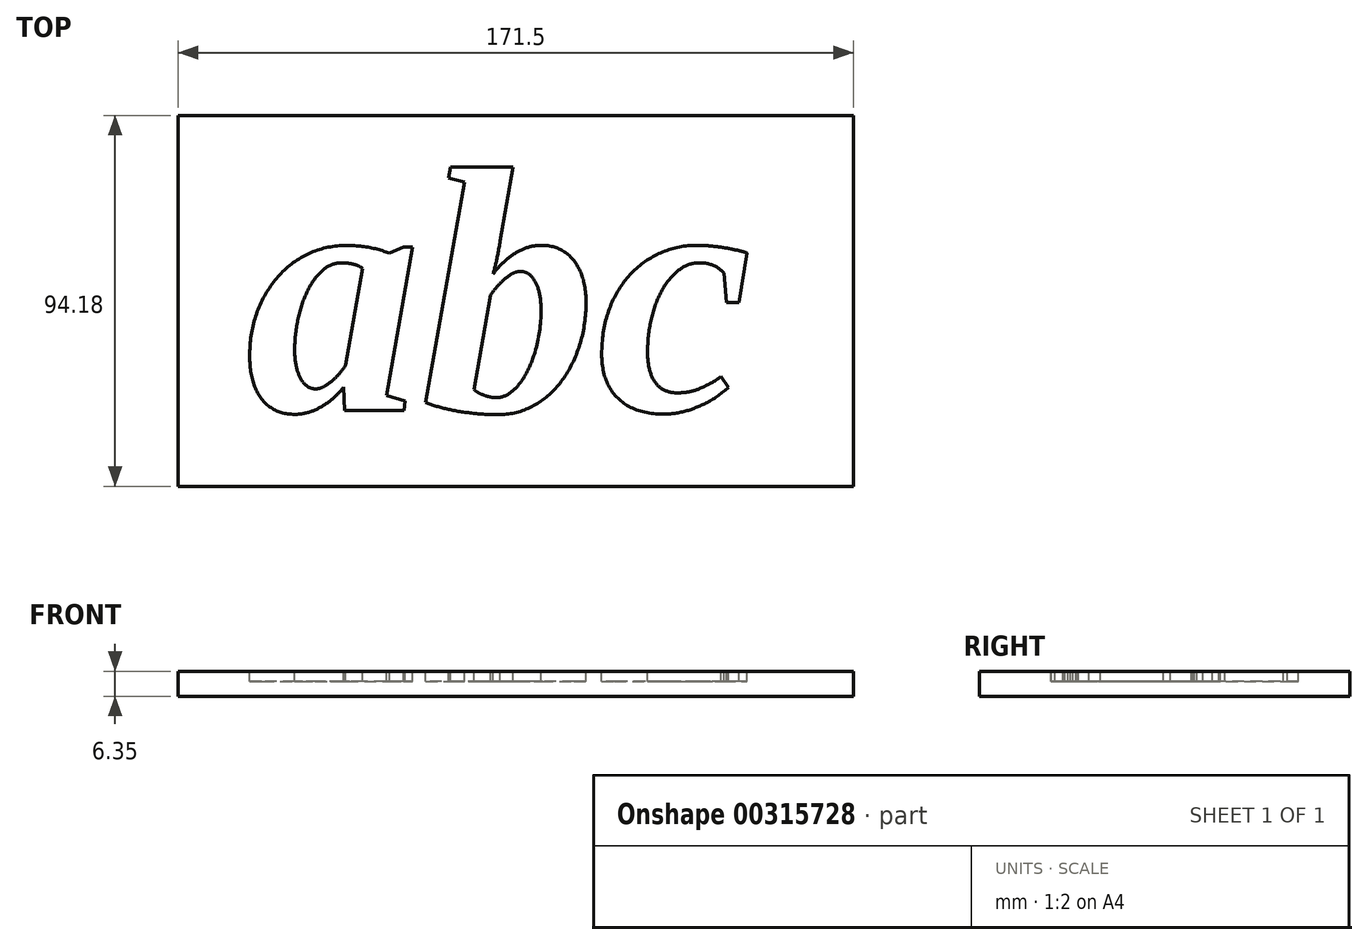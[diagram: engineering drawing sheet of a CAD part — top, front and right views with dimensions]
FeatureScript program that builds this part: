
annotation { "Feature Type Name" : "Feature", "Feature Type Description" : "" }
export const myFeature = defineFeature(function(context is Context, id is Id, definition is map)
    precondition{}
    {
        {
            var Q0;
            Q0=qCreatedBy(makeId("Top.planeOp"),FACE);
            var sketch = newSketch(context, id + "F0", { "sketchPlane" : qUnion([Q0])});
            skText(sketch, "E0", { "text": "abc", "fontName": "Tinos-BoldItalic.ttf"});
            const initialGuessF0  = {"E0": [-0.06912, -0.03573, 1, 0, 0.0642]};
            skSetInitialGuess(sketch, initialGuessF0);
            skSolve(sketch);
        }
        {
            var Q0;
            Q0 = qSketchRegion(id + "F0", true);
            extrude(context, id + "F1", {"entities" : qUnion([Q0]), "oppositeDirection" : true, "depth" : 2.54 * mm});
        }
        {
            var Q0;
            Q0=qCreatedBy(makeId("Top.planeOp"),FACE);
            var sketch = newSketch(context, id + "F2", { "sketchPlane" : qUnion([Q0])});
            skLineSegment(sketch, "E1.bottom", {"start": v(-86.22, 39.24) * mm, "end": v(85.28, 39.24) * mm});
            skLineSegment(sketch, "E1.top", {"start": v(-86.22, -54.94) * mm, "end": v(85.28, -54.94) * mm});
            skLineSegment(sketch, "E1.left", {"start": v(-86.22, 39.24) * mm, "end": v(-86.22, -54.94) * mm});
            skLineSegment(sketch, "E1.right", {"start": v(85.28, 39.24) * mm, "end": v(85.28, -54.94) * mm});
            skSolve(sketch);
        }
        {
            var Q0;
            Q0 = qSketchRegion(id + "F2", true);
            extrude(context, id + "F3", {"entities" : qUnion([Q0]), "oppositeDirection" : true, "depth" : 6.35 * mm});
        }
        {
            var Q0;
            Q0=makeQuery(id+"F1.opExtrude","SWEPT_BODY",BODY,{"disambiguationData":[OSD([sQuery(id+"F0.wireOp",EDGE,"E0.sketch_text.stroke-0"),sQuery(id+"F0.wireOp",EDGE,"E0.sketch_text.stroke-1"),sQuery(id+"F0.wireOp",EDGE,"E0.sketch_text.stroke-2"),sQuery(id+"F0.wireOp",EDGE,"E0.sketch_text.stroke-3"),sQuery(id+"F0.wireOp",EDGE,"E0.sketch_text.stroke-4"),sQuery(id+"F0.wireOp",EDGE,"E0.sketch_text.stroke-5"),sQuery(id+"F0.wireOp",EDGE,"E0.sketch_text.stroke-6"),sQuery(id+"F0.wireOp",EDGE,"E0.sketch_text.stroke-7"),sQuery(id+"F0.wireOp",EDGE,"E0.sketch_text.stroke-8"),sQuery(id+"F0.wireOp",EDGE,"E0.sketch_text.stroke-9"),sQuery(id+"F0.wireOp",EDGE,"E0.sketch_text.stroke-10"),sQuery(id+"F0.wireOp",EDGE,"E0.sketch_text.stroke-11"),sQuery(id+"F0.wireOp",EDGE,"E0.sketch_text.stroke-12"),sQuery(id+"F0.wireOp",EDGE,"E0.sketch_text.stroke-13"),sQuery(id+"F0.wireOp",EDGE,"E0.sketch_text.stroke-14"),sQuery(id+"F0.wireOp",EDGE,"E0.sketch_text.stroke-15"),sQuery(id+"F0.wireOp",EDGE,"E0.sketch_text.stroke-16"),sQuery(id+"F0.wireOp",EDGE,"E0.sketch_text.stroke-17"),sQuery(id+"F0.wireOp",EDGE,"E0.sketch_text.stroke-18"),sQuery(id+"F0.wireOp",EDGE,"E0.sketch_text.stroke-19"),sQuery(id+"F0.wireOp",EDGE,"E0.sketch_text.stroke-20"),sQuery(id+"F0.wireOp",EDGE,"E0.sketch_text.stroke-21"),sQuery(id+"F0.wireOp",EDGE,"E0.sketch_text.stroke-22"),sQuery(id+"F0.wireOp",EDGE,"E0.sketch_text.stroke-23")])]});
            var Q1;
            Q1=makeQuery(id+"F1.opExtrude","SWEPT_BODY",BODY,{"disambiguationData":[OSD([sQuery(id+"F0.wireOp",EDGE,"E0.sketch_text.stroke-24"),sQuery(id+"F0.wireOp",EDGE,"E0.sketch_text.stroke-25"),sQuery(id+"F0.wireOp",EDGE,"E0.sketch_text.stroke-26"),sQuery(id+"F0.wireOp",EDGE,"E0.sketch_text.stroke-27"),sQuery(id+"F0.wireOp",EDGE,"E0.sketch_text.stroke-28"),sQuery(id+"F0.wireOp",EDGE,"E0.sketch_text.stroke-29"),sQuery(id+"F0.wireOp",EDGE,"E0.sketch_text.stroke-30"),sQuery(id+"F0.wireOp",EDGE,"E0.sketch_text.stroke-31"),sQuery(id+"F0.wireOp",EDGE,"E0.sketch_text.stroke-32"),sQuery(id+"F0.wireOp",EDGE,"E0.sketch_text.stroke-33"),sQuery(id+"F0.wireOp",EDGE,"E0.sketch_text.stroke-34"),sQuery(id+"F0.wireOp",EDGE,"E0.sketch_text.stroke-35"),sQuery(id+"F0.wireOp",EDGE,"E0.sketch_text.stroke-36"),sQuery(id+"F0.wireOp",EDGE,"E0.sketch_text.stroke-37"),sQuery(id+"F0.wireOp",EDGE,"E0.sketch_text.stroke-38"),sQuery(id+"F0.wireOp",EDGE,"E0.sketch_text.stroke-39"),sQuery(id+"F0.wireOp",EDGE,"E0.sketch_text.stroke-40"),sQuery(id+"F0.wireOp",EDGE,"E0.sketch_text.stroke-41"),sQuery(id+"F0.wireOp",EDGE,"E0.sketch_text.stroke-42"),sQuery(id+"F0.wireOp",EDGE,"E0.sketch_text.stroke-43"),sQuery(id+"F0.wireOp",EDGE,"E0.sketch_text.stroke-44"),sQuery(id+"F0.wireOp",EDGE,"E0.sketch_text.stroke-45"),sQuery(id+"F0.wireOp",EDGE,"E0.sketch_text.stroke-46"),sQuery(id+"F0.wireOp",EDGE,"E0.sketch_text.stroke-47"),sQuery(id+"F0.wireOp",EDGE,"E0.sketch_text.stroke-48")])]});
            var Q2;
            Q2=makeQuery(id+"F1.opExtrude","SWEPT_BODY",BODY,{"disambiguationData":[OSD([sQuery(id+"F0.wireOp",EDGE,"E0.sketch_text.stroke-49"),sQuery(id+"F0.wireOp",EDGE,"E0.sketch_text.stroke-50"),sQuery(id+"F0.wireOp",EDGE,"E0.sketch_text.stroke-51"),sQuery(id+"F0.wireOp",EDGE,"E0.sketch_text.stroke-52"),sQuery(id+"F0.wireOp",EDGE,"E0.sketch_text.stroke-53"),sQuery(id+"F0.wireOp",EDGE,"E0.sketch_text.stroke-54"),sQuery(id+"F0.wireOp",EDGE,"E0.sketch_text.stroke-55"),sQuery(id+"F0.wireOp",EDGE,"E0.sketch_text.stroke-56"),sQuery(id+"F0.wireOp",EDGE,"E0.sketch_text.stroke-57"),sQuery(id+"F0.wireOp",EDGE,"E0.sketch_text.stroke-58"),sQuery(id+"F0.wireOp",EDGE,"E0.sketch_text.stroke-59"),sQuery(id+"F0.wireOp",EDGE,"E0.sketch_text.stroke-60"),sQuery(id+"F0.wireOp",EDGE,"E0.sketch_text.stroke-61"),sQuery(id+"F0.wireOp",EDGE,"E0.sketch_text.stroke-62"),sQuery(id+"F0.wireOp",EDGE,"E0.sketch_text.stroke-63"),sQuery(id+"F0.wireOp",EDGE,"E0.sketch_text.stroke-64"),sQuery(id+"F0.wireOp",EDGE,"E0.sketch_text.stroke-65"),sQuery(id+"F0.wireOp",EDGE,"E0.sketch_text.stroke-66"),sQuery(id+"F0.wireOp",EDGE,"E0.sketch_text.stroke-67"),sQuery(id+"F0.wireOp",EDGE,"E0.sketch_text.stroke-68"),sQuery(id+"F0.wireOp",EDGE,"E0.sketch_text.stroke-69")])]});
            var Q3;
            Q3=makeQuery(id+"F3.opExtrude","SWEPT_BODY",BODY,{"disambiguationData":[OSD([sQuery(id+"F2.wireOp",EDGE,"E1.bottom"),sQuery(id+"F2.wireOp",EDGE,"E1.top"),sQuery(id+"F2.wireOp",EDGE,"E1.left"),sQuery(id+"F2.wireOp",EDGE,"E1.right")])]});
            booleanBodies(context, id + "F4", {"operationType" : BooleanOperationType.SUBTRACTION, "tools" : qUnion([Q0, Q1, Q2]), "targets" : qUnion([Q3])});
        }
    });
